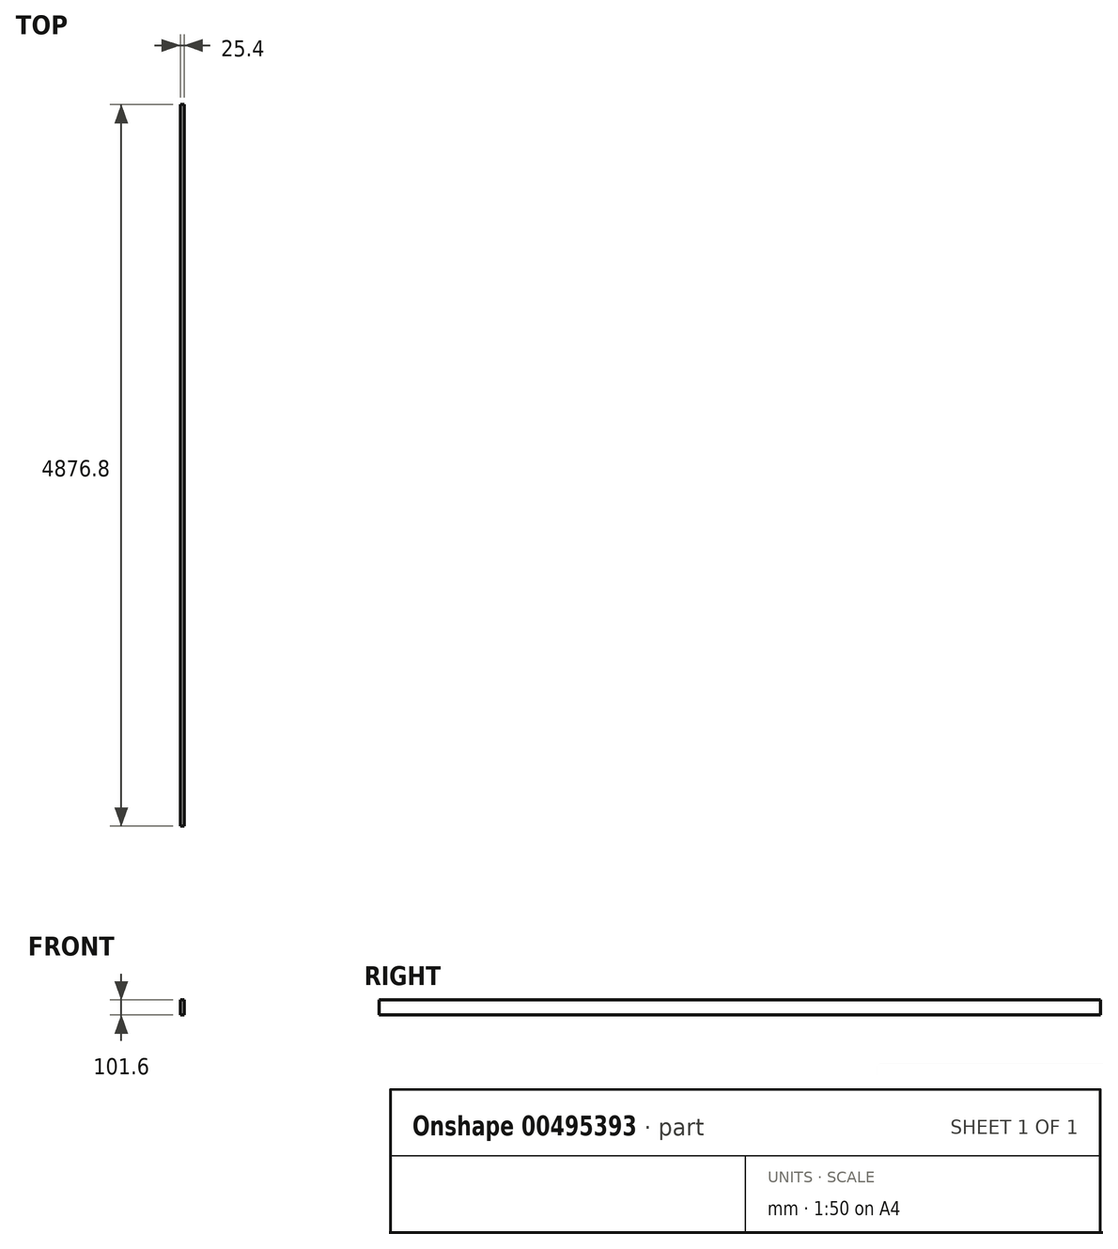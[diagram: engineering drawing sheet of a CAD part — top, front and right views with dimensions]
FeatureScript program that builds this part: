
annotation { "Feature Type Name" : "Feature", "Feature Type Description" : "" }
export const myFeature = defineFeature(function(context is Context, id is Id, definition is map)
    precondition{}
    {
        {
            var Q0;
            Q0=qCreatedBy(makeId("Front.planeOp"),FACE);
            var sketch = newSketch(context, id + "F0", { "sketchPlane" : qUnion([Q0])});
            skLineSegment(sketch, "E0.bottom", {"start": v(0, 0) * mm, "end": v(25.4, 0) * mm});
            skLineSegment(sketch, "E0.top", {"start": v(0, 101.6) * mm, "end": v(25.4, 101.6) * mm});
            skLineSegment(sketch, "E0.left", {"start": v(0, 0) * mm, "end": v(0, 101.6) * mm});
            skLineSegment(sketch, "E0.right", {"start": v(25.4, 0) * mm, "end": v(25.4, 101.6) * mm});
            skSolve(sketch);
        }
        {
            var Q0;
            Q0 = qSketchRegion(id + "F0", true);
            extrude(context, id + "F1", {"entities" : qUnion([Q0]), "depth" : 4876.8 * mm, "offsetDistance" : 25.4 * mm});
        }
    });
